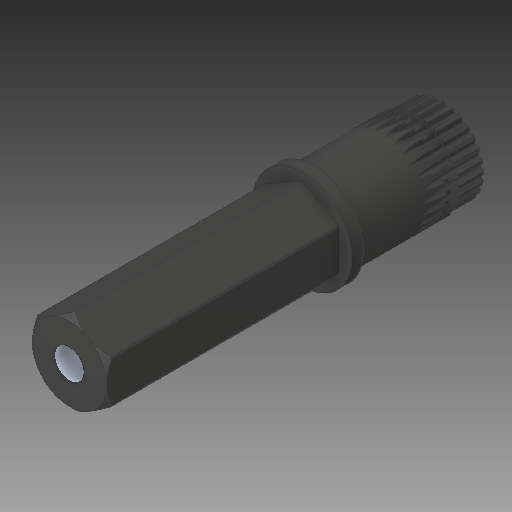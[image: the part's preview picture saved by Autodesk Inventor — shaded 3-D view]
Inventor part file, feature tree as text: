
AUTODESK INVENTOR PART (.ipt)
format: ipt  version: 2017 SP1 (Build 210196100, 196)  size: 1,423,360 bytes
history: native  units: in
note: dims shown in document units (in); Inventor stores cm internally (conversion verified against a paired STEP export)
features: fillet x1
ambient origin geometry x8: Origin, YZ Plane, XZ Plane, XY Plane, X Axis, Y Axis, Z Axis, Center Point
bodies: Solid1 (feature_tree)
feature tree (1):
  fillet  "Fillet5"  [1 undecoded]
note: 1 required parameter value undecoded (feature->parameter linkage not recoverable at this tier; creation-order binding heuristic only, values carry confidence <= 0.55)
